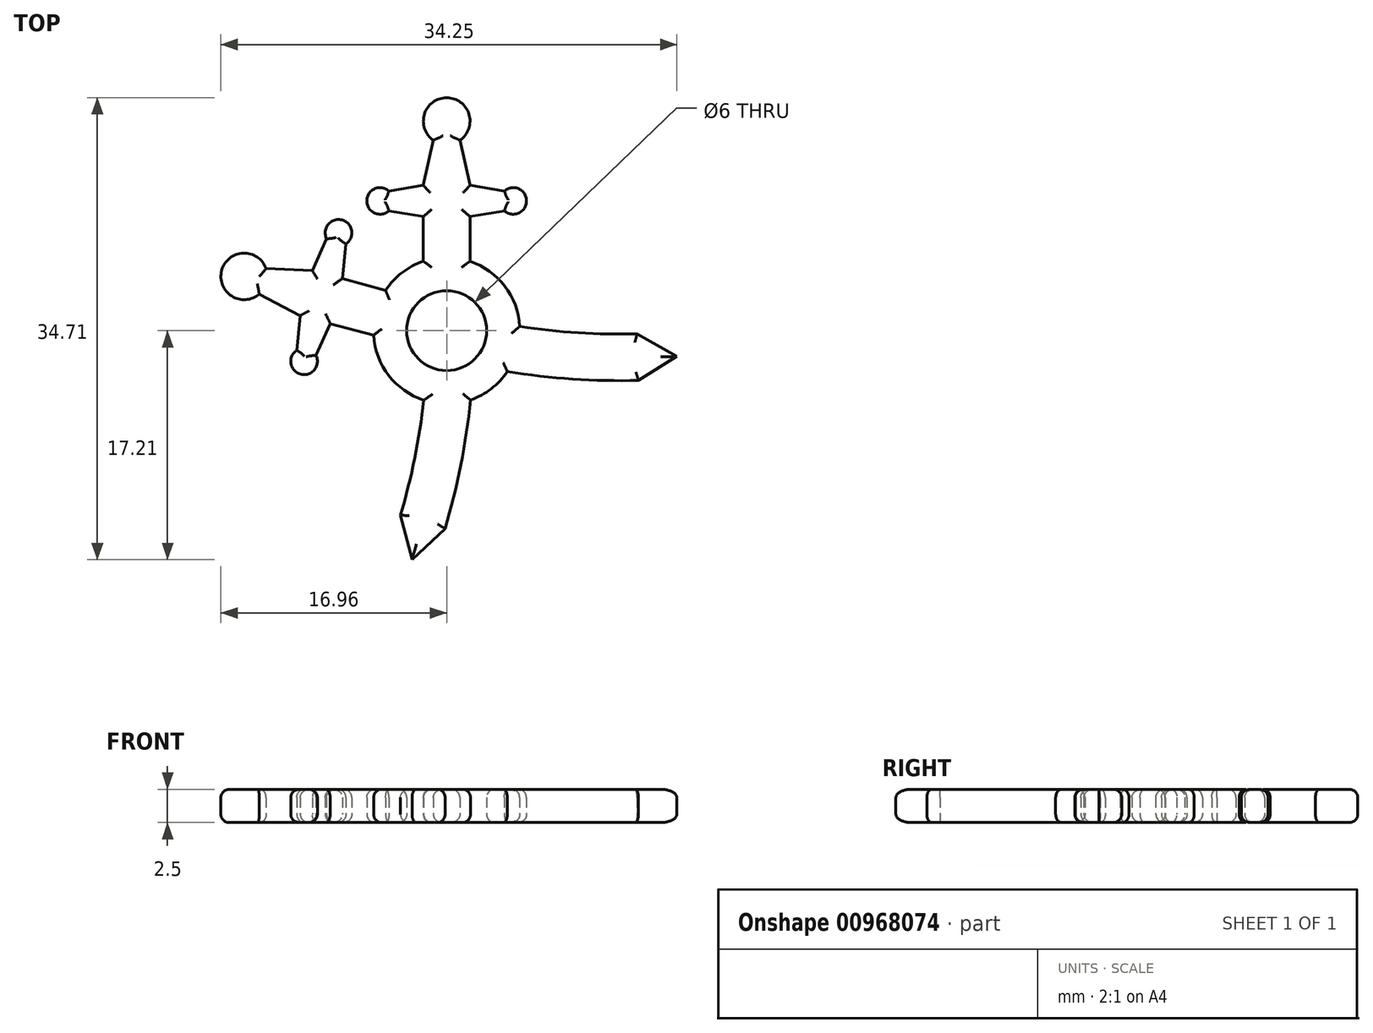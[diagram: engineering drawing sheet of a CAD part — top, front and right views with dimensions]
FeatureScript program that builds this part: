
annotation { "Feature Type Name" : "Feature", "Feature Type Description" : "" }
export const myFeature = defineFeature(function(context is Context, id is Id, definition is map)
    precondition{}
    {
        {
            assignVariable(context, id + "F0", {"name" : "thickness", "anyValue" : 2.5});
        }
        {
            var Q0;
            Q0=qCreatedBy(makeId("Front.planeOp"),FACE);
            var sketch = newSketch(context, id + "F1", { "sketchPlane" : qUnion([Q0])});
            skLineSegment(sketch, "E0", {"start": v(0, -0.36) * mm, "end": v(0, 0.53) * mm, "construction": true});
            skSolve(sketch);
        }
        {
            var Q0;
            Q0=qCreatedBy(makeId("Top.planeOp"),FACE);
            var sketch = newSketch(context, id + "F2", { "sketchPlane" : qUnion([Q0])});
            skArc(sketch, "E1", {"start": v(-1.75, 5.21) * mm, "mid": v(-5.5, -0.05) * mm, "end": v(-1.65, -5.25) * mm});
            skArc(sketch, "E2", {"start": v(0, 3) * mm, "mid": v(-3, 0) * mm, "end": v(0, -3) * mm});
            skLineSegment(sketch, "E3.left", {"start": v(0, 15.75) * mm, "end": v(0, 5.5) * mm});
            skLineSegment(sketch, "E4.left", {"start": v(0, 9.75) * mm, "end": v(0, 5.5) * mm});
            skLineSegment(sketch, "E5.left", {"start": v(0, 15.75) * mm, "end": v(0, 9.75) * mm});
            skArc(sketch, "E6", {"start": v(0, 17.5) * mm, "mid": v(-1.67, 16.27) * mm, "end": v(-1, 14.31) * mm});
            skLineSegment(sketch, "E7", {"start": v(-1.75, 5.21) * mm, "end": v(-1.75, 8.58) * mm});
            skLineSegment(sketch, "E8", {"start": v(-1.75, 8.58) * mm, "end": v(-4.34, 9) * mm});
            skLineSegment(sketch, "E9", {"start": v(-4.34, 10.5) * mm, "end": v(-1.75, 10.92) * mm});
            skLineSegment(sketch, "E10", {"start": v(-1.75, 10.92) * mm, "end": v(-1, 14.31) * mm});
            skArc(sketch, "E11", {"start": v(-4.34, 10.5) * mm, "mid": v(-6, 9.75) * mm, "end": v(-4.34, 9) * mm});
            skLineSegment(sketch, "E12", {"start": v(-5, 9.75) * mm, "end": v(0, 9.75) * mm, "construction": true});
            skPoint(sketch, "E13", {"position": v(-4.34, 10.5) * mm});
            skPoint(sketch, "E14", {"position": v(-4.34, 9) * mm});
            skLineSegment(sketch, "E15", {"start": v(-1.75, 10.92) * mm, "end": v(-1.75, 8.58) * mm, "construction": true});
            skLineSegment(sketch, "E16", {"start": v(0, 5.5) * mm, "end": v(0, 3) * mm});
            skLineSegment(sketch, "E17.trimOffspring", {"start": v(0, -3) * mm, "end": v(0, -5.5) * mm});
            skPoint(sketch, "E18.orphan", {"position": v(-5, 10.4) * mm});
            skPoint(sketch, "E19.orphan", {"position": v(-5, 9.1) * mm});
            skLineSegment(sketch, "E20", {"start": v(0, 17.5) * mm, "end": v(0, 14) * mm});
            skArc(sketch, "E21", {"start": v(0, -5.5) * mm, "mid": v(-0.83, -5.44) * mm, "end": v(-1.65, -5.25) * mm});
            skSolve(sketch);
        }
        {
            var Q0;
            Q0=qCreatedBy(makeId("Top.planeOp"),FACE);
            var sketch = newSketch(context, id + "F3", { "sketchPlane" : qUnion([Q0])});
            skArc(sketch, "E22", {"start": v(0, -5.5) * mm, "mid": v(-0.64, -9.7) * mm, "end": v(-1.64, -13.84) * mm, "construction": true});
            skCircle(sketch, "E23", {"center": v(0, 0) * mm, "radius": 5.5 * mm, "construction": true});
            skArc(sketch, "E24.0", {"start": v(-1.69, -4.83) * mm, "mid": v(-2.37, -9.4) * mm, "end": v(-3.47, -13.88) * mm});
            skArc(sketch, "E25.0", {"start": v(1.8, -5.2) * mm, "mid": v(1.07, -10.08) * mm, "end": v(-0.12, -14.88) * mm});
            skLineSegment(sketch, "E26", {"start": v(-1.64, -13.84) * mm, "end": v(-2.6, -17.2) * mm, "construction": true});
            skLineSegment(sketch, "E27", {"start": v(-3.47, -13.88) * mm, "end": v(-2.6, -17.2) * mm});
            skLineSegment(sketch, "E28", {"start": v(-2.6, -17.2) * mm, "end": v(-0.12, -14.88) * mm});
            skArc(sketch, "E29", {"start": v(-1.73, -5.22) * mm, "mid": v(0.03, -5.5) * mm, "end": v(1.8, -5.2) * mm});
            skLineSegment(sketch, "E30", {"start": v(-1.73, -5.22) * mm, "end": v(-1.69, -4.83) * mm});
            skSolve(sketch);
        }
        {
            var Q0;
            Q0=qCreatedBy(makeId("Top.planeOp"),FACE);
            var sketch = newSketch(context, id + "F4", { "sketchPlane" : qUnion([Q0])});
            skLineSegment(sketch, "E31", {"start": v(9.28, 7.12) * mm, "end": v(-9.28, -7.12) * mm, "construction": true});
            skSolve(sketch);
        }
        {
            var Q0;
            Q0=sQuery(id+"F4.wireOp",EDGE,"E31");
            cPlane(context, id + "F5", {"entities" : qUnion([Q0]), "cplaneType" : CPlaneType.MID_PLANE, "offset" : 25 * mm, "width" : 150 * mm, "height" : 150 * mm});
        }
        {
            var Q0;
            Q0=qSketchRegion(id+"F2",true);
            extrude(context, id + "F6", {"entities" : qUnion([Q0]), "depth" : (getVariable(context, 'thickness')) * mm, "offsetDistance" : 25 * mm});
        }
        {
            var Q0;
            Q0=makeQuery(id+"F6.opExtrude","SWEPT_BODY",BODY,{"disambiguationData":[OSD([sQuery(id+"F2.wireOp",EDGE,"E1"),sQuery(id+"F2.wireOp",EDGE,"E2"),sQuery(id+"F2.wireOp",EDGE,"E4.left"),sQuery(id+"F2.wireOp",EDGE,"E5.left"),sQuery(id+"F2.wireOp",EDGE,"E6"),sQuery(id+"F2.wireOp",EDGE,"orh27yux-9RoH-fIbY-CIuJ-KNKRVuCyGNKg"),sQuery(id+"F2.wireOp",EDGE,"87CVhjRQ-Wfej-MxDc-ivz2-TprIwiOqAEPk"),sQuery(id+"F2.wireOp",EDGE,"OpRQFFEB-QS2l-NP3g-x3Nt-C4CFWvN4k208"),sQuery(id+"F2.wireOp",EDGE,"E7"),sQuery(id+"F2.wireOp",EDGE,"E8"),sQuery(id+"F2.wireOp",EDGE,"E9"),sQuery(id+"F2.wireOp",EDGE,"E10"),sQuery(id+"F2.wireOp",EDGE,"E11"),sQuery(id+"F2.wireOp",EDGE,"E16"),sQuery(id+"F2.wireOp",EDGE,"E17.trimOffspring"),sQuery(id+"F2.wireOp",EDGE,"E20")])]});
            var Q1;
            Q1=qCreatedBy(makeId("Right.planeOp"),FACE);
            mirror(context, id + "F7", {"entities" : qUnion([Q0]), "mirrorPlane" : qUnion([Q1])});
        }
        {
            var Q0;
            Q0 = qSketchRegion(id + "F3", true);
            extrude(context, id + "F8", {"entities" : qUnion([Q0]), "operationType" : NewBodyOperationType.ADD, "depth" : (getVariable(context, 'thickness')) * mm, "offsetDistance" : 25 * mm});
        }
        {
            var Q0;
            Q0=makeQuery(id+"F6.opExtrude","SWEPT_BODY",BODY,{"disambiguationData":[OSD([sQuery(id+"F2.wireOp",EDGE,"E1"),sQuery(id+"F2.wireOp",EDGE,"E2"),sQuery(id+"F2.wireOp",EDGE,"E4.left"),sQuery(id+"F2.wireOp",EDGE,"E5.left"),sQuery(id+"F2.wireOp",EDGE,"E6"),sQuery(id+"F2.wireOp",EDGE,"E7"),sQuery(id+"F2.wireOp",EDGE,"E8"),sQuery(id+"F2.wireOp",EDGE,"E9"),sQuery(id+"F2.wireOp",EDGE,"E10"),sQuery(id+"F2.wireOp",EDGE,"E11"),sQuery(id+"F2.wireOp",EDGE,"E16"),sQuery(id+"F2.wireOp",EDGE,"E17.trimOffspring"),sQuery(id+"F2.wireOp",EDGE,"E20"),sQuery(id+"F2.wireOp",EDGE,"E21")])]});
            var Q1;
            Q1=qCreatedBy(id+"F5.planeOp",FACE);
            mirror(context, id + "F9", {"operationType" : NewBodyOperationType.ADD, "entities" : qUnion([Q0]), "mirrorPlane" : qUnion([Q1])});
        }
        {
            var Q0;
            {var subQ0=sQuery(id+"FF2sNrfYVvZR24D_0.1.F2.wireOp",EDGE,"E1");Q0=makeQuery(id+"FdIG1sQytHje1PW_3.opBoolean","MERGE",FACE,{"derivedFrom":[makeQuery(id+"F6.opExtrude","CAP_FACE",FACE,{"disambiguationData":[OSD([sQuery(id+"F2.wireOp",EDGE,"E1"),sQuery(id+"F2.wireOp",EDGE,"E2"),sQuery(id+"F2.wireOp",EDGE,"v7ZpJoOp-nusw-QLSr-9RbJ-bJiLEr91LXo7"),sQuery(id+"F2.wireOp",EDGE,"vIL4BcYA-nMGL-yGJ3-ga3U-vjNq2aGALbEF"),sQuery(id+"F2.wireOp",EDGE,"ded36fca-b699-4c9c-8e45-1f6b24a533490.MirrorCS"),sQuery(id+"F2.wireOp",EDGE,"113ruoVQ-M4KL-XzLS-Qnhd-6DCeCMZ775Q7"),sQuery(id+"F2.wireOp",EDGE,"E4.right"),sQuery(id+"F2.wireOp",EDGE,"n4rSyH3h-1NrD-ScX6-riRr-7jgFtbDAqfhq"),sQuery(id+"F2.wireOp",EDGE,"E6"),sQuery(id+"F2.wireOp",EDGE,"ce75eabf-e140-428c-91a5-72ef84fb78f10.MirrorCS"),sQuery(id+"F2.wireOp",EDGE,"14d6e69c-b8a8-4542-9b5b-1f979469ac310.MirrorCS"),sQuery(id+"F2.wireOp",EDGE,"fbd9c578-6410-4f49-8b6d-a704f98f1ad50.MirrorCS"),sQuery(id+"F2.wireOp",EDGE,"a38b117b-53eb-4dc5-a93f-0499820181ec0.MirrorCS"),sQuery(id+"F2.wireOp",EDGE,"e87fbdaf-6be0-438d-a6e1-7897cd8f2fb90.MirrorC"),sQuery(id+"F2.wireOp",EDGE,"3ac102b6-e1ec-459a-9db9-2dd38266f8ac0.MirrorCS"),sQuery(id+"F2.wireOp",EDGE,"a1574d3b-a5dd-4b71-a9ed-16474a823ba0.trimOffspring"),sQuery(id+"F2.wireOp",EDGE,"586c9f6e-5c17-4a3d-9881-5d2215f88811.trimOffspring")])],"isStart":true}),makeQuery(id+"F6.opExtrude","CAP_FACE",FACE,{"disambiguationData":[OSD([subQ0,sQuery(id+"FF2sNrfYVvZR24D_0.1.F2.wireOp",EDGE,"vIL4BcYA-nMGL-yGJ3-ga3U-vjNq2aGALbEF"),sQuery(id+"FF2sNrfYVvZR24D_0.1.F2.wireOp",EDGE,"ded36fca-b699-4c9c-8e45-1f6b24a533490.MirrorCS"),sQuery(id+"FF2sNrfYVvZR24D_0.1.F2.wireOp",EDGE,"113ruoVQ-M4KL-XzLS-Qnhd-6DCeCMZ775Q7"),sQuery(id+"FF2sNrfYVvZR24D_0.1.F2.wireOp",EDGE,"E4.right"),sQuery(id+"FF2sNrfYVvZR24D_0.1.F2.wireOp",EDGE,"n4rSyH3h-1NrD-ScX6-riRr-7jgFtbDAqfhq"),sQuery(id+"FF2sNrfYVvZR24D_0.1.F2.wireOp",EDGE,"E6"),sQuery(id+"FF2sNrfYVvZR24D_0.1.F2.wireOp",EDGE,"ce75eabf-e140-428c-91a5-72ef84fb78f10.MirrorCS"),sQuery(id+"FF2sNrfYVvZR24D_0.1.F2.wireOp",EDGE,"14d6e69c-b8a8-4542-9b5b-1f979469ac310.MirrorCS"),sQuery(id+"FF2sNrfYVvZR24D_0.1.F2.wireOp",EDGE,"fbd9c578-6410-4f49-8b6d-a704f98f1ad50.MirrorCS"),sQuery(id+"FF2sNrfYVvZR24D_0.1.F2.wireOp",EDGE,"a38b117b-53eb-4dc5-a93f-0499820181ec0.MirrorCS"),sQuery(id+"FF2sNrfYVvZR24D_0.1.F2.wireOp",EDGE,"e87fbdaf-6be0-438d-a6e1-7897cd8f2fb90.MirrorC")])],"isStart":true}),makeQuery(id+"F6.opExtrude","CAP_FACE",FACE,{"disambiguationData":[OSD([subQ0,sQuery(id+"FF2sNrfYVvZR24D_0.1.F2.wireOp",EDGE,"v7ZpJoOp-nusw-QLSr-9RbJ-bJiLEr91LXo7"),sQuery(id+"FF2sNrfYVvZR24D_0.1.F2.wireOp",EDGE,"3ac102b6-e1ec-459a-9db9-2dd38266f8ac0.MirrorCS"),sQuery(id+"FF2sNrfYVvZR24D_0.1.F2.wireOp",EDGE,"a1574d3b-a5dd-4b71-a9ed-16474a823ba0.trimOffspring"),sQuery(id+"FF2sNrfYVvZR24D_0.1.F2.wireOp",EDGE,"586c9f6e-5c17-4a3d-9881-5d2215f88811.trimOffspring")])],"isStart":true})]});}
            var Q1;
            {var subQ0=sQuery(id+"FF2sNrfYVvZR24D_0.1.F2.wireOp",EDGE,"E1");Q1=makeQuery(id+"FdIG1sQytHje1PW_3.opBoolean","MERGE",FACE,{"derivedFrom":[makeQuery(id+"F6.opExtrude","CAP_FACE",FACE,{"disambiguationData":[OSD([sQuery(id+"F2.wireOp",EDGE,"E1"),sQuery(id+"F2.wireOp",EDGE,"E2"),sQuery(id+"F2.wireOp",EDGE,"v7ZpJoOp-nusw-QLSr-9RbJ-bJiLEr91LXo7"),sQuery(id+"F2.wireOp",EDGE,"vIL4BcYA-nMGL-yGJ3-ga3U-vjNq2aGALbEF"),sQuery(id+"F2.wireOp",EDGE,"ded36fca-b699-4c9c-8e45-1f6b24a533490.MirrorCS"),sQuery(id+"F2.wireOp",EDGE,"113ruoVQ-M4KL-XzLS-Qnhd-6DCeCMZ775Q7"),sQuery(id+"F2.wireOp",EDGE,"E4.right"),sQuery(id+"F2.wireOp",EDGE,"n4rSyH3h-1NrD-ScX6-riRr-7jgFtbDAqfhq"),sQuery(id+"F2.wireOp",EDGE,"E6"),sQuery(id+"F2.wireOp",EDGE,"ce75eabf-e140-428c-91a5-72ef84fb78f10.MirrorCS"),sQuery(id+"F2.wireOp",EDGE,"14d6e69c-b8a8-4542-9b5b-1f979469ac310.MirrorCS"),sQuery(id+"F2.wireOp",EDGE,"fbd9c578-6410-4f49-8b6d-a704f98f1ad50.MirrorCS"),sQuery(id+"F2.wireOp",EDGE,"a38b117b-53eb-4dc5-a93f-0499820181ec0.MirrorCS"),sQuery(id+"F2.wireOp",EDGE,"e87fbdaf-6be0-438d-a6e1-7897cd8f2fb90.MirrorC"),sQuery(id+"F2.wireOp",EDGE,"3ac102b6-e1ec-459a-9db9-2dd38266f8ac0.MirrorCS"),sQuery(id+"F2.wireOp",EDGE,"a1574d3b-a5dd-4b71-a9ed-16474a823ba0.trimOffspring"),sQuery(id+"F2.wireOp",EDGE,"586c9f6e-5c17-4a3d-9881-5d2215f88811.trimOffspring")])],"isStart":false}),makeQuery(id+"F6.opExtrude","CAP_FACE",FACE,{"disambiguationData":[OSD([subQ0,sQuery(id+"FF2sNrfYVvZR24D_0.1.F2.wireOp",EDGE,"vIL4BcYA-nMGL-yGJ3-ga3U-vjNq2aGALbEF"),sQuery(id+"FF2sNrfYVvZR24D_0.1.F2.wireOp",EDGE,"ded36fca-b699-4c9c-8e45-1f6b24a533490.MirrorCS"),sQuery(id+"FF2sNrfYVvZR24D_0.1.F2.wireOp",EDGE,"113ruoVQ-M4KL-XzLS-Qnhd-6DCeCMZ775Q7"),sQuery(id+"FF2sNrfYVvZR24D_0.1.F2.wireOp",EDGE,"E4.right"),sQuery(id+"FF2sNrfYVvZR24D_0.1.F2.wireOp",EDGE,"n4rSyH3h-1NrD-ScX6-riRr-7jgFtbDAqfhq"),sQuery(id+"FF2sNrfYVvZR24D_0.1.F2.wireOp",EDGE,"E6"),sQuery(id+"FF2sNrfYVvZR24D_0.1.F2.wireOp",EDGE,"ce75eabf-e140-428c-91a5-72ef84fb78f10.MirrorCS"),sQuery(id+"FF2sNrfYVvZR24D_0.1.F2.wireOp",EDGE,"14d6e69c-b8a8-4542-9b5b-1f979469ac310.MirrorCS"),sQuery(id+"FF2sNrfYVvZR24D_0.1.F2.wireOp",EDGE,"fbd9c578-6410-4f49-8b6d-a704f98f1ad50.MirrorCS"),sQuery(id+"FF2sNrfYVvZR24D_0.1.F2.wireOp",EDGE,"a38b117b-53eb-4dc5-a93f-0499820181ec0.MirrorCS"),sQuery(id+"FF2sNrfYVvZR24D_0.1.F2.wireOp",EDGE,"e87fbdaf-6be0-438d-a6e1-7897cd8f2fb90.MirrorC")])],"isStart":false}),makeQuery(id+"F6.opExtrude","CAP_FACE",FACE,{"disambiguationData":[OSD([subQ0,sQuery(id+"FF2sNrfYVvZR24D_0.1.F2.wireOp",EDGE,"v7ZpJoOp-nusw-QLSr-9RbJ-bJiLEr91LXo7"),sQuery(id+"FF2sNrfYVvZR24D_0.1.F2.wireOp",EDGE,"3ac102b6-e1ec-459a-9db9-2dd38266f8ac0.MirrorCS"),sQuery(id+"FF2sNrfYVvZR24D_0.1.F2.wireOp",EDGE,"a1574d3b-a5dd-4b71-a9ed-16474a823ba0.trimOffspring"),sQuery(id+"FF2sNrfYVvZR24D_0.1.F2.wireOp",EDGE,"586c9f6e-5c17-4a3d-9881-5d2215f88811.trimOffspring")])],"isStart":false})]});}
            fillet(context, id + "F10", {"entities" : qUnion([Q0, Q1]), "radius" : (getVariable(context, 'thickness') / 4) * mm, "tangentPropagation" : true, "allowEdgeOverflow" : false});
        }
    });
